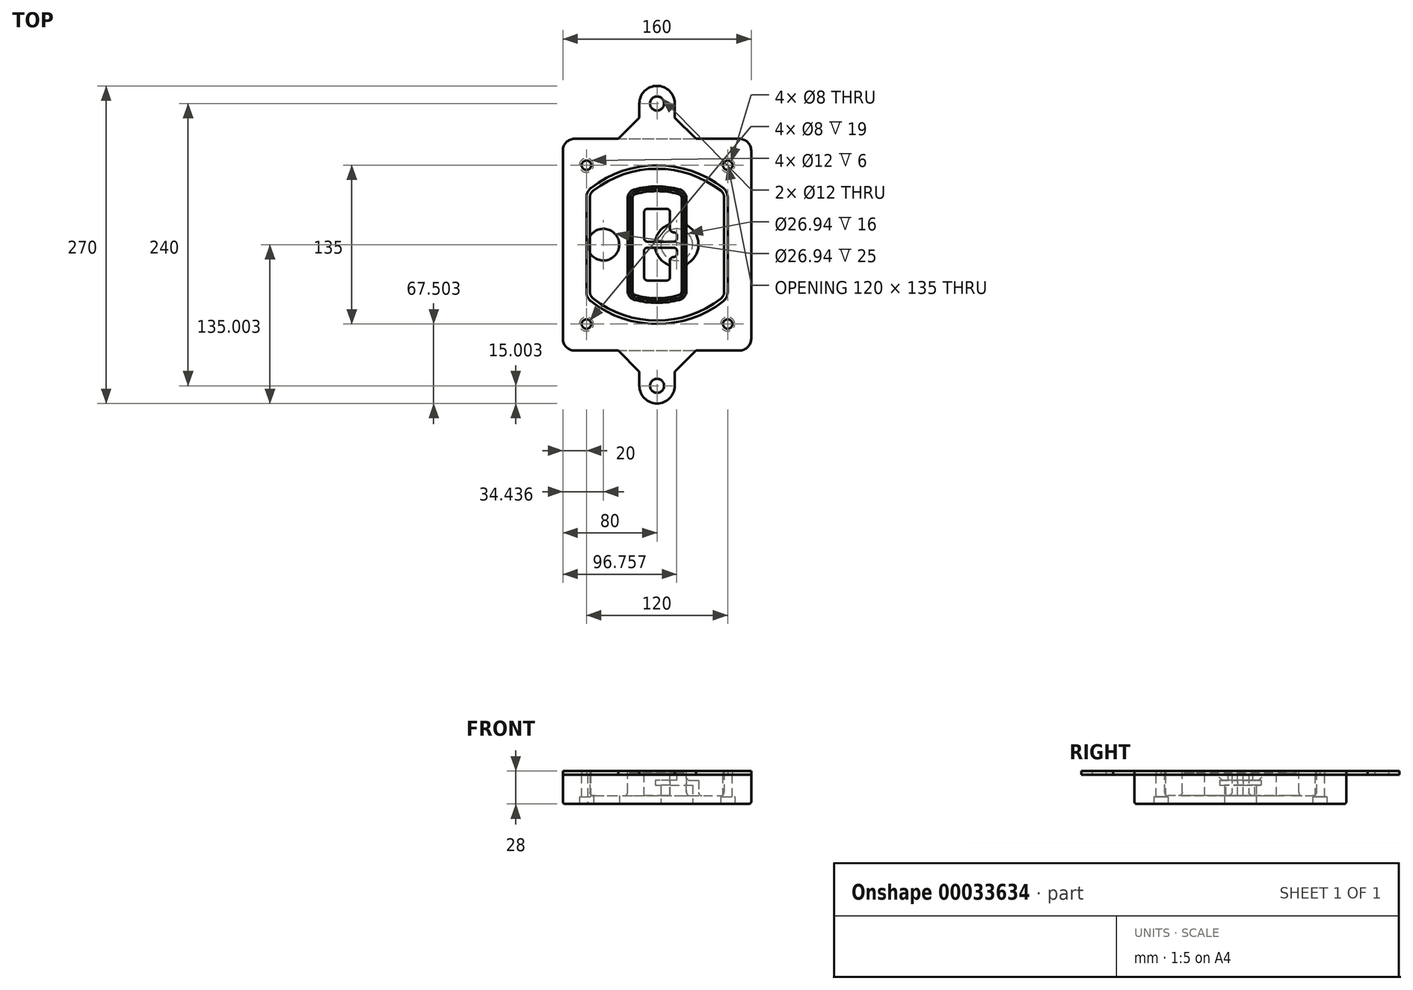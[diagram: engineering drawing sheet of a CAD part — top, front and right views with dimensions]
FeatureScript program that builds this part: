
annotation { "Feature Type Name" : "Feature", "Feature Type Description" : "" }
export const myFeature = defineFeature(function(context is Context, id is Id, definition is map)
    precondition{}
    {
        {
            var Q0;
            Q0=qCreatedBy(makeId("Top.planeOp"),FACE);
            var sketch = newSketch(context, id + "F0", { "sketchPlane" : qUnion([Q0])});
            skPoint(sketch, "E0.rect.middle", {"position": v(0, 0) * mm});
            skLineSegment(sketch, "E1.bottom", {"start": v(24.05, 28.38) * mm, "end": v(164.05, 28.38) * mm});
            skLineSegment(sketch, "E1.top", {"start": v(24.05, 208.38) * mm, "end": v(164.05, 208.38) * mm});
            skLineSegment(sketch, "E1.left", {"start": v(14.05, 38.38) * mm, "end": v(14.05, 198.38) * mm});
            skLineSegment(sketch, "E1.right", {"start": v(174.05, 38.38) * mm, "end": v(174.05, 198.38) * mm});
            skLineSegment(sketch, "E2", {"start": v(14.05, 208.38) * mm, "end": v(174.05, 28.38) * mm, "construction": true});
            skLineSegment(sketch, "E3", {"start": v(174.05, 208.38) * mm, "end": v(14.05, 28.38) * mm, "construction": true});
            skCircle(sketch, "E4", {"center": v(34.05, 185.88) * mm, "radius": 4 * mm});
            skCircle(sketch, "E5", {"center": v(154.05, 185.88) * mm, "radius": 4 * mm});
            skCircle(sketch, "E6", {"center": v(154.05, 50.88) * mm, "radius": 4 * mm});
            skCircle(sketch, "E7", {"center": v(34.05, 50.88) * mm, "radius": 4 * mm});
            skLineSegment(sketch, "E8", {"start": v(34.05, 185.88) * mm, "end": v(154.05, 185.88) * mm, "construction": true});
            skLineSegment(sketch, "E9", {"start": v(154.05, 185.88) * mm, "end": v(154.05, 50.88) * mm, "construction": true});
            skLineSegment(sketch, "E10", {"start": v(154.05, 50.88) * mm, "end": v(34.05, 50.88) * mm, "construction": true});
            skLineSegment(sketch, "E11", {"start": v(34.05, 50.88) * mm, "end": v(34.05, 185.88) * mm, "construction": true});
            skLineSegment(sketch, "E12", {"start": v(34.05, 158.68) * mm, "end": v(34.05, 78.09) * mm});
            skLineSegment(sketch, "E13", {"start": v(154.05, 158.68) * mm, "end": v(154.05, 78.09) * mm});
            skArc(sketch, "E14", {"start": v(150.2, 166.56) * mm, "mid": v(94.05, 185.88) * mm, "end": v(37.9, 166.56) * mm});
            skArc(sketch, "E15", {"start": v(37.9, 70.2) * mm, "mid": v(94.05, 50.88) * mm, "end": v(150.2, 70.2) * mm});
            skLineSegment(sketch, "E16", {"start": v(34.05, 118.38) * mm, "end": v(154.05, 118.38) * mm, "construction": true});
            skPoint(sketch, "E17.visualSharp", {"position": v(34.05, 73.38) * mm});
            skArc(sketch, "E17.filletArc", {"start": v(34.05, 78.09) * mm, "mid": v(35.06, 73.7) * mm, "end": v(37.9, 70.2) * mm});
            skPoint(sketch, "E18.visualSharp", {"position": v(34.05, 163.38) * mm});
            skArc(sketch, "E18.filletArc", {"start": v(37.9, 166.56) * mm, "mid": v(35.06, 163.06) * mm, "end": v(34.05, 158.68) * mm});
            skPoint(sketch, "E19.visualSharp", {"position": v(154.05, 163.38) * mm});
            skArc(sketch, "E19.filletArc", {"start": v(154.05, 158.68) * mm, "mid": v(153.04, 163.06) * mm, "end": v(150.2, 166.56) * mm});
            skPoint(sketch, "E20.visualSharp", {"position": v(154.05, 73.38) * mm});
            skArc(sketch, "E20.filletArc", {"start": v(150.2, 70.2) * mm, "mid": v(153.04, 73.7) * mm, "end": v(154.05, 78.09) * mm});
            skPoint(sketch, "E21.visualSharp", {"position": v(14.05, 208.38) * mm});
            skArc(sketch, "E21.filletArc", {"start": v(24.05, 208.38) * mm, "mid": v(16.98, 205.45) * mm, "end": v(14.05, 198.38) * mm});
            skPoint(sketch, "E22.visualSharp", {"position": v(174.05, 208.38) * mm});
            skArc(sketch, "E22.filletArc", {"start": v(174.05, 198.38) * mm, "mid": v(171.12, 205.45) * mm, "end": v(164.05, 208.38) * mm});
            skPoint(sketch, "E23.visualSharp", {"position": v(174.05, 28.38) * mm});
            skArc(sketch, "E23.filletArc", {"start": v(164.05, 28.38) * mm, "mid": v(171.12, 31.31) * mm, "end": v(174.05, 38.38) * mm});
            skPoint(sketch, "E24.visualSharp", {"position": v(14.05, 28.38) * mm});
            skArc(sketch, "E24.filletArc", {"start": v(14.05, 38.38) * mm, "mid": v(16.98, 31.31) * mm, "end": v(24.05, 28.38) * mm});
            skArc(sketch, "E25.0", {"start": v(151.05, 158.68) * mm, "mid": v(150.34, 161.75) * mm, "end": v(148.36, 164.2) * mm});
            skLineSegment(sketch, "E25.1", {"start": v(151.05, 158.68) * mm, "end": v(151.05, 78.09) * mm});
            skArc(sketch, "E25.2", {"start": v(148.36, 72.57) * mm, "mid": v(150.34, 75.02) * mm, "end": v(151.05, 78.09) * mm});
            skArc(sketch, "E25.3", {"start": v(39.74, 72.57) * mm, "mid": v(94.05, 53.88) * mm, "end": v(148.36, 72.57) * mm});
            skArc(sketch, "E25.4", {"start": v(37.05, 78.09) * mm, "mid": v(37.76, 75.02) * mm, "end": v(39.74, 72.57) * mm});
            skArc(sketch, "E25.5", {"start": v(148.36, 164.2) * mm, "mid": v(94.05, 182.88) * mm, "end": v(39.74, 164.2) * mm});
            skLineSegment(sketch, "E25.6", {"start": v(37.05, 158.68) * mm, "end": v(37.05, 78.09) * mm});
            skArc(sketch, "E25.7", {"start": v(39.74, 164.2) * mm, "mid": v(37.76, 161.75) * mm, "end": v(37.05, 158.68) * mm});
            skArc(sketch, "E26.0", {"start": v(35.43, 169.71) * mm, "mid": v(31.47, 164.82) * mm, "end": v(30.05, 158.68) * mm});
            skArc(sketch, "E26.1", {"start": v(152.67, 169.71) * mm, "mid": v(94.05, 189.88) * mm, "end": v(35.43, 169.71) * mm});
            skArc(sketch, "E26.2", {"start": v(158.05, 158.68) * mm, "mid": v(156.63, 164.82) * mm, "end": v(152.67, 169.71) * mm});
            skLineSegment(sketch, "E26.3", {"start": v(158.05, 158.68) * mm, "end": v(158.05, 78.09) * mm});
            skArc(sketch, "E26.4", {"start": v(152.67, 67.05) * mm, "mid": v(156.63, 71.95) * mm, "end": v(158.05, 78.09) * mm});
            skLineSegment(sketch, "E26.5", {"start": v(30.05, 158.68) * mm, "end": v(30.05, 78.09) * mm});
            skArc(sketch, "E26.6", {"start": v(35.43, 67.05) * mm, "mid": v(94.05, 46.88) * mm, "end": v(152.67, 67.05) * mm});
            skArc(sketch, "E26.7", {"start": v(30.05, 78.09) * mm, "mid": v(31.47, 71.95) * mm, "end": v(35.43, 67.05) * mm});
            skSolve(sketch);
        }
        {
            var Q0;
            Q0=makeQuery(id+"F0.imprint","IMPRINT",FACE,{"disambiguationData":[TD([[makeQuery(id+"F0.imprint","IMPRINT",EDGE,{"derivedFrom":sQuery(id+"F0.wireOp",EDGE,"E1.bottom")}),1.0]])]});
            var Q1;
            Q1=makeQuery(id+"F0.imprint","IMPRINT",FACE,{"disambiguationData":[TD([[makeQuery(id+"F0.imprint","IMPRINT",EDGE,{"derivedFrom":sQuery(id+"F0.wireOp",EDGE,"E12")}),1.0]])]});
            var Q2;
            Q2=makeQuery(id+"F0.imprint","IMPRINT",FACE,{"disambiguationData":[TD([[makeQuery(id+"F0.imprint","IMPRINT",EDGE,{"derivedFrom":sQuery(id+"F0.wireOp",EDGE,"E25.0")}),1.0]])]});
            var Q3;
            Q3=makeQuery(id+"F0.imprint","IMPRINT",FACE,{"disambiguationData":[TD([[makeQuery(id+"F0.imprint","IMPRINT",EDGE,{"derivedFrom":sQuery(id+"F0.wireOp",EDGE,"E12")}),-1.0]])]});
            extrude(context, id + "F1", {"entities" : qUnion([Q0, Q1, Q2, Q3]), "oppositeDirection" : true, "depth" : 25 * mm});
        }
        {
            var Q0;
            Q0=makeQuery(id+"F0.imprint","IMPRINT",FACE,{"disambiguationData":[TD([[makeQuery(id+"F0.imprint","IMPRINT",EDGE,{"derivedFrom":sQuery(id+"F0.wireOp",EDGE,"E12")}),1.0]])]});
            extrude(context, id + "F2", {"entities" : qUnion([Q0]), "operationType" : NewBodyOperationType.ADD, "depth" : 3 * mm});
        }
        {
            var Q0;
            Q0=makeQuery(id+"F0.imprint","IMPRINT",FACE,{"disambiguationData":[TD([[makeQuery(id+"F0.imprint","IMPRINT",EDGE,{"derivedFrom":sQuery(id+"F0.wireOp",EDGE,"E25.0")}),1.0]])]});
            extrude(context, id + "F3", {"entities" : qUnion([Q0]), "operationType" : NewBodyOperationType.REMOVE, "oppositeDirection" : true, "depth" : 18 * mm});
        }
        {
            var Q0;
            Q0=makeQuery(id+"F2.opExtrude","CAP_FACE",FACE,{"disambiguationData":[OSD([sQuery(id+"F0.wireOp",EDGE,"E12"),sQuery(id+"F0.wireOp",EDGE,"E13"),sQuery(id+"F0.wireOp",EDGE,"E14"),sQuery(id+"F0.wireOp",EDGE,"E15"),sQuery(id+"F0.wireOp",EDGE,"E17.filletArc"),sQuery(id+"F0.wireOp",EDGE,"E18.filletArc"),sQuery(id+"F0.wireOp",EDGE,"E19.filletArc"),sQuery(id+"F0.wireOp",EDGE,"E20.filletArc"),sQuery(id+"F0.wireOp",EDGE,"E25.0"),sQuery(id+"F0.wireOp",EDGE,"E25.1"),sQuery(id+"F0.wireOp",EDGE,"E25.2"),sQuery(id+"F0.wireOp",EDGE,"E25.3"),sQuery(id+"F0.wireOp",EDGE,"E25.4"),sQuery(id+"F0.wireOp",EDGE,"E25.5"),sQuery(id+"F0.wireOp",EDGE,"E25.6"),sQuery(id+"F0.wireOp",EDGE,"E25.7")])],"isStart":false});
            var sketch = newSketch(context, id + "F4", { "sketchPlane" : qUnion([Q0])});
            skArc(sketch, "E27.0", {"start": v(74.97, 71.41) * mm, "mid": v(94.05, 68.88) * mm, "end": v(113.13, 71.41) * mm});
            skArc(sketch, "E28.0", {"start": v(113.13, 165.35) * mm, "mid": v(94.05, 167.88) * mm, "end": v(74.97, 165.35) * mm});
            skLineSegment(sketch, "E29", {"start": v(69.05, 157.63) * mm, "end": v(69.05, 79.14) * mm});
            skLineSegment(sketch, "E30", {"start": v(119.05, 157.63) * mm, "end": v(119.05, 79.14) * mm});
            skLineSegment(sketch, "E31", {"start": v(69.05, 163.48) * mm, "end": v(119.05, 163.48) * mm, "construction": true});
            skLineSegment(sketch, "E32", {"start": v(69.05, 73.28) * mm, "end": v(119.05, 73.28) * mm, "construction": true});
            skPoint(sketch, "E33.visualSharp", {"position": v(69.05, 163.48) * mm});
            skArc(sketch, "E33.filletArc", {"start": v(74.97, 165.35) * mm, "mid": v(70.7, 162.5) * mm, "end": v(69.05, 157.63) * mm});
            skPoint(sketch, "E34.visualSharp", {"position": v(119.05, 163.48) * mm});
            skArc(sketch, "E34.filletArc", {"start": v(119.05, 157.63) * mm, "mid": v(117.4, 162.5) * mm, "end": v(113.13, 165.35) * mm});
            skPoint(sketch, "E35.visualSharp", {"position": v(119.05, 73.28) * mm});
            skArc(sketch, "E35.filletArc", {"start": v(113.13, 71.41) * mm, "mid": v(117.4, 74.27) * mm, "end": v(119.05, 79.14) * mm});
            skPoint(sketch, "E36.visualSharp", {"position": v(69.05, 73.28) * mm});
            skArc(sketch, "E36.filletArc", {"start": v(69.05, 79.14) * mm, "mid": v(70.7, 74.27) * mm, "end": v(74.97, 71.41) * mm});
            skArc(sketch, "E37.0", {"start": v(148.36, 164.2) * mm, "mid": v(94.05, 182.88) * mm, "end": v(39.74, 164.2) * mm});
            skArc(sketch, "E37.1", {"start": v(39.74, 164.2) * mm, "mid": v(37.76, 161.75) * mm, "end": v(37.05, 158.68) * mm});
            skLineSegment(sketch, "E37.2", {"start": v(37.05, 158.68) * mm, "end": v(37.05, 78.09) * mm});
            skArc(sketch, "E37.3", {"start": v(37.05, 78.09) * mm, "mid": v(37.76, 75.02) * mm, "end": v(39.74, 72.57) * mm});
            skArc(sketch, "E37.4", {"start": v(39.74, 72.57) * mm, "mid": v(94.05, 53.88) * mm, "end": v(148.36, 72.57) * mm});
            skArc(sketch, "E37.5", {"start": v(148.36, 72.57) * mm, "mid": v(150.34, 75.02) * mm, "end": v(151.05, 78.09) * mm});
            skLineSegment(sketch, "E37.6", {"start": v(151.05, 158.68) * mm, "end": v(151.05, 78.09) * mm});
            skArc(sketch, "E37.7", {"start": v(151.05, 158.68) * mm, "mid": v(150.34, 161.75) * mm, "end": v(148.36, 164.2) * mm});
            skLineSegment(sketch, "E38.0", {"start": v(117.05, 157.63) * mm, "end": v(117.05, 79.14) * mm});
            skArc(sketch, "E38.1", {"start": v(112.61, 73.34) * mm, "mid": v(115.81, 75.49) * mm, "end": v(117.05, 79.14) * mm});
            skArc(sketch, "E38.2", {"start": v(75.49, 73.34) * mm, "mid": v(94.05, 70.88) * mm, "end": v(112.61, 73.34) * mm});
            skArc(sketch, "E38.3", {"start": v(71.05, 79.14) * mm, "mid": v(72.29, 75.49) * mm, "end": v(75.49, 73.34) * mm});
            skLineSegment(sketch, "E38.4", {"start": v(71.05, 157.63) * mm, "end": v(71.05, 79.14) * mm});
            skArc(sketch, "E38.5", {"start": v(117.05, 157.63) * mm, "mid": v(115.81, 161.28) * mm, "end": v(112.61, 163.42) * mm});
            skArc(sketch, "E38.6", {"start": v(75.49, 163.42) * mm, "mid": v(72.29, 161.28) * mm, "end": v(71.05, 157.63) * mm});
            skArc(sketch, "E38.7", {"start": v(112.61, 163.42) * mm, "mid": v(94.05, 165.88) * mm, "end": v(75.49, 163.42) * mm});
            skArc(sketch, "E39.0", {"start": v(115.05, 157.63) * mm, "mid": v(114.23, 160.06) * mm, "end": v(112.1, 161.5) * mm});
            skLineSegment(sketch, "E39.1", {"start": v(115.05, 157.63) * mm, "end": v(115.05, 79.14) * mm});
            skArc(sketch, "E39.2", {"start": v(112.1, 75.27) * mm, "mid": v(114.23, 76.7) * mm, "end": v(115.05, 79.14) * mm});
            skArc(sketch, "E39.3", {"start": v(76, 75.27) * mm, "mid": v(94.05, 72.88) * mm, "end": v(112.1, 75.27) * mm});
            skArc(sketch, "E39.4", {"start": v(73.05, 79.14) * mm, "mid": v(73.87, 76.7) * mm, "end": v(76, 75.27) * mm});
            skArc(sketch, "E39.5", {"start": v(112.1, 161.5) * mm, "mid": v(94.05, 163.88) * mm, "end": v(76, 161.5) * mm});
            skLineSegment(sketch, "E39.6", {"start": v(73.05, 157.63) * mm, "end": v(73.05, 79.14) * mm});
            skArc(sketch, "E39.7", {"start": v(76, 161.5) * mm, "mid": v(73.87, 160.06) * mm, "end": v(73.05, 157.63) * mm});
            skLineSegment(sketch, "E40", {"start": v(69.05, 118.38) * mm, "end": v(119.05, 118.38) * mm, "construction": true});
            skLineSegment(sketch, "E41", {"start": v(83.05, 123.88) * mm, "end": v(83.05, 145.88) * mm});
            skLineSegment(sketch, "E42", {"start": v(86.05, 148.88) * mm, "end": v(102.05, 148.88) * mm});
            skLineSegment(sketch, "E43", {"start": v(105.05, 145.88) * mm, "end": v(105.05, 131.88) * mm});
            skLineSegment(sketch, "E44", {"start": v(108.05, 128.88) * mm, "end": v(108.05, 128.88) * mm});
            skLineSegment(sketch, "E45", {"start": v(111.05, 125.88) * mm, "end": v(111.05, 123.88) * mm});
            skLineSegment(sketch, "E46", {"start": v(108.05, 120.88) * mm, "end": v(86.05, 120.88) * mm});
            skPoint(sketch, "E47.visualSharp", {"position": v(83.05, 148.88) * mm});
            skArc(sketch, "E47.filletArc", {"start": v(86.05, 148.88) * mm, "mid": v(83.93, 148) * mm, "end": v(83.05, 145.88) * mm});
            skPoint(sketch, "E48.visualSharp", {"position": v(105.05, 148.88) * mm});
            skArc(sketch, "E48.filletArc", {"start": v(105.05, 145.88) * mm, "mid": v(104.17, 148) * mm, "end": v(102.05, 148.88) * mm});
            skPoint(sketch, "E49.visualSharp", {"position": v(105.05, 128.88) * mm});
            skArc(sketch, "E49.filletArc", {"start": v(105.05, 131.88) * mm, "mid": v(105.93, 129.76) * mm, "end": v(108.05, 128.88) * mm});
            skPoint(sketch, "E50.visualSharp", {"position": v(111.05, 128.88) * mm});
            skArc(sketch, "E50.filletArc", {"start": v(111.05, 125.88) * mm, "mid": v(110.17, 128) * mm, "end": v(108.05, 128.88) * mm});
            skPoint(sketch, "E51.visualSharp", {"position": v(111.05, 120.88) * mm});
            skArc(sketch, "E51.filletArc", {"start": v(108.05, 120.88) * mm, "mid": v(110.17, 121.76) * mm, "end": v(111.05, 123.88) * mm});
            skPoint(sketch, "E52.visualSharp", {"position": v(83.05, 120.88) * mm});
            skArc(sketch, "E52.filletArc", {"start": v(83.05, 123.88) * mm, "mid": v(83.93, 121.76) * mm, "end": v(86.05, 120.88) * mm});
            skLineSegment(sketch, "E53.0.MirrorCS", {"start": v(108.05, 115.88) * mm, "end": v(86.05, 115.88) * mm});
            skArc(sketch, "E54.0.MirrorCS", {"start": v(83.05, 112.88) * mm, "mid": v(83.93, 115) * mm, "end": v(86.05, 115.88) * mm});
            skLineSegment(sketch, "E55.0.MirrorCS", {"start": v(83.05, 112.88) * mm, "end": v(83.05, 90.88) * mm});
            skArc(sketch, "E56.0.MirrorCS", {"start": v(86.05, 87.88) * mm, "mid": v(83.93, 88.76) * mm, "end": v(83.05, 90.88) * mm});
            skLineSegment(sketch, "E57.0.MirrorCS", {"start": v(86.05, 87.88) * mm, "end": v(102.05, 87.88) * mm});
            skArc(sketch, "E58.0.MirrorCS", {"start": v(105.05, 90.88) * mm, "mid": v(104.17, 88.76) * mm, "end": v(102.05, 87.88) * mm});
            skLineSegment(sketch, "E59.0.MirrorCS", {"start": v(105.05, 90.88) * mm, "end": v(105.05, 104.88) * mm});
            skArc(sketch, "E60.0.MirrorCS", {"start": v(105.05, 104.88) * mm, "mid": v(105.93, 107) * mm, "end": v(108.05, 107.88) * mm});
            skArc(sketch, "E61.0.MirrorCS", {"start": v(111.05, 110.88) * mm, "mid": v(110.17, 108.76) * mm, "end": v(108.05, 107.88) * mm});
            skLineSegment(sketch, "E62.0.MirrorCS", {"start": v(111.05, 110.88) * mm, "end": v(111.05, 112.88) * mm});
            skArc(sketch, "E63.0.MirrorCS", {"start": v(108.05, 115.88) * mm, "mid": v(110.17, 115) * mm, "end": v(111.05, 112.88) * mm});
            skSolve(sketch);
        }
        {
            var Q0;
            Q0=makeQuery(id+"F4.imprint","IMPRINT",FACE,{"disambiguationData":[TD([[makeQuery(id+"F4.imprint","IMPRINT",EDGE,{"derivedFrom":sQuery(id+"F4.wireOp",EDGE,"E27.0")}),1.0]])]});
            var Q1;
            Q1=makeQuery(id+"F4.imprint","IMPRINT",FACE,{"disambiguationData":[TD([[makeQuery(id+"F4.imprint","IMPRINT",EDGE,{"derivedFrom":sQuery(id+"F4.wireOp",EDGE,"E38.0")}),-1.0]])]});
            var Q2;
            Q2=makeQuery(id+"F4.imprint","IMPRINT",FACE,{"disambiguationData":[TD([[makeQuery(id+"F4.imprint","IMPRINT",EDGE,{"derivedFrom":sQuery(id+"F4.wireOp",EDGE,"E39.0")}),1.0]])]});
            extrude(context, id + "F5", {"entities" : qUnion([Q0, Q1, Q2]), "operationType" : NewBodyOperationType.ADD, "endBound" : BoundingType.UP_TO_NEXT, "oppositeDirection" : true, "depth" : 25 * mm});
        }
        {
            var Q0;
            Q0=makeQuery(id+"F4.imprint","IMPRINT",FACE,{"disambiguationData":[TD([[makeQuery(id+"F4.imprint","IMPRINT",EDGE,{"derivedFrom":sQuery(id+"F4.wireOp",EDGE,"E38.0")}),-1.0]])]});
            extrude(context, id + "F6", {"entities" : qUnion([Q0]), "operationType" : NewBodyOperationType.REMOVE, "oppositeDirection" : true, "depth" : 2 * mm});
        }
        {
            var Q0;
            Q0=makeQuery(id+"F1.opExtrude","CAP_FACE",FACE,{"disambiguationData":[OSD([sQuery(id+"F0.wireOp",EDGE,"E1.bottom"),sQuery(id+"F0.wireOp",EDGE,"E1.top"),sQuery(id+"F0.wireOp",EDGE,"E1.left"),sQuery(id+"F0.wireOp",EDGE,"E1.right"),sQuery(id+"F0.wireOp",EDGE,"E4"),sQuery(id+"F0.wireOp",EDGE,"E5"),sQuery(id+"F0.wireOp",EDGE,"E6"),sQuery(id+"F0.wireOp",EDGE,"E7"),sQuery(id+"F0.wireOp",EDGE,"E21.filletArc"),sQuery(id+"F0.wireOp",EDGE,"E22.filletArc"),sQuery(id+"F0.wireOp",EDGE,"E23.filletArc"),sQuery(id+"F0.wireOp",EDGE,"E24.filletArc")])],"isStart":false});
            var sketch = newSketch(context, id + "F7", { "sketchPlane" : qUnion([Q0])});
            skCircle(sketch, "E64", {"center": v(110.8, -118.38) * mm, "radius": 13.47 * mm});
            skCircle(sketch, "E65", {"center": v(48.49, -118.38) * mm, "radius": 13.47 * mm});
            skLineSegment(sketch, "E66", {"start": v(174.05, -118.38) * mm, "end": v(14.05, -118.38) * mm});
            skCircle(sketch, "E67", {"center": v(110.8, -118.38) * mm, "radius": 18.47 * mm});
            skCircle(sketch, "E68", {"center": v(154.05, -185.88) * mm, "radius": 6 * mm});
            skCircle(sketch, "E69", {"center": v(34.05, -185.88) * mm, "radius": 6 * mm});
            skCircle(sketch, "E70", {"center": v(34.05, -50.88) * mm, "radius": 6 * mm});
            skCircle(sketch, "E71", {"center": v(154.05, -50.88) * mm, "radius": 6 * mm});
            skSolve(sketch);
        }
        {
            var Q0;
            {var subQ1=sQuery(id+"F7.wireOp",EDGE,"E66");var subQ4=sQuery(id+"F7.wireOp",EDGE,"E64");var subQ6=makeQuery(id+"F7.imprint","INTERSECT",VERTEX,{"disambiguationData":[OD(0.0)],"derivedFrom":[subQ4,subQ1]});Q0=makeQuery(id+"F7.imprint","IMPRINT",FACE,{"disambiguationData":[TD([[makeQuery(id+"F7.imprint","IMPRINT",EDGE,{"disambiguationData":[TD([[subQ6,-1.0]])],"derivedFrom":subQ4}),-1.0]])]});}
            var Q1;
            {var subQ0=sQuery(id+"F7.wireOp",EDGE,"E66");var subQ1=sQuery(id+"F7.wireOp",EDGE,"E64");var subQ3=makeQuery(id+"F7.imprint","INTERSECT",VERTEX,{"disambiguationData":[OD(0.0)],"derivedFrom":[subQ1,subQ0]});Q1=makeQuery(id+"F7.imprint","IMPRINT",FACE,{"disambiguationData":[TD([[makeQuery(id+"F7.imprint","IMPRINT",EDGE,{"disambiguationData":[TD([[subQ3,-1.0]])],"derivedFrom":subQ1}),1.0]])]});}
            var Q2;
            {var subQ0=sQuery(id+"F7.wireOp",EDGE,"E66");var subQ1=sQuery(id+"F7.wireOp",EDGE,"E64");var subQ3=makeQuery(id+"F7.imprint","INTERSECT",VERTEX,{"disambiguationData":[OD(0.0)],"derivedFrom":[subQ1,subQ0]});Q2=makeQuery(id+"F7.imprint","IMPRINT",FACE,{"disambiguationData":[TD([[makeQuery(id+"F7.imprint","IMPRINT",EDGE,{"disambiguationData":[TD([[subQ3,1.0]])],"derivedFrom":subQ1}),1.0]])]});}
            var Q3;
            {var subQ1=sQuery(id+"F7.wireOp",EDGE,"E66");var subQ4=sQuery(id+"F7.wireOp",EDGE,"E64");var subQ6=makeQuery(id+"F7.imprint","INTERSECT",VERTEX,{"disambiguationData":[OD(0.0)],"derivedFrom":[subQ4,subQ1]});Q3=makeQuery(id+"F7.imprint","IMPRINT",FACE,{"disambiguationData":[TD([[makeQuery(id+"F7.imprint","IMPRINT",EDGE,{"disambiguationData":[TD([[subQ6,1.0]])],"derivedFrom":subQ4}),-1.0]])]});}
            extrude(context, id + "F8", {"entities" : qUnion([Q0, Q1, Q2, Q3]), "operationType" : NewBodyOperationType.ADD, "oppositeDirection" : true, "depth" : 20 * mm});
        }
        {
            var Q0;
            {var subQ0=sQuery(id+"F7.wireOp",EDGE,"E66");var subQ1=sQuery(id+"F7.wireOp",EDGE,"E64");var subQ3=makeQuery(id+"F7.imprint","INTERSECT",VERTEX,{"disambiguationData":[OD(0.0)],"derivedFrom":[subQ1,subQ0]});Q0=makeQuery(id+"F7.imprint","IMPRINT",FACE,{"disambiguationData":[TD([[makeQuery(id+"F7.imprint","IMPRINT",EDGE,{"disambiguationData":[TD([[subQ3,-1.0]])],"derivedFrom":subQ1}),1.0]])]});}
            var Q1;
            {var subQ0=sQuery(id+"F7.wireOp",EDGE,"E66");var subQ1=sQuery(id+"F7.wireOp",EDGE,"E64");var subQ3=makeQuery(id+"F7.imprint","INTERSECT",VERTEX,{"disambiguationData":[OD(0.0)],"derivedFrom":[subQ1,subQ0]});Q1=makeQuery(id+"F7.imprint","IMPRINT",FACE,{"disambiguationData":[TD([[makeQuery(id+"F7.imprint","IMPRINT",EDGE,{"disambiguationData":[TD([[subQ3,1.0]])],"derivedFrom":subQ1}),1.0]])]});}
            extrude(context, id + "F9", {"entities" : qUnion([Q0, Q1]), "operationType" : NewBodyOperationType.REMOVE, "oppositeDirection" : true, "depth" : 16 * mm});
        }
        {
            var Q0;
            {var subQ0=sQuery(id+"F7.wireOp",EDGE,"E66");var subQ1=sQuery(id+"F7.wireOp",EDGE,"E65");var subQ3=makeQuery(id+"F7.imprint","INTERSECT",VERTEX,{"disambiguationData":[OD(0.0)],"derivedFrom":[subQ1,subQ0]});Q0=makeQuery(id+"F7.imprint","IMPRINT",FACE,{"disambiguationData":[TD([[makeQuery(id+"F7.imprint","IMPRINT",EDGE,{"disambiguationData":[TD([[subQ3,-1.0]])],"derivedFrom":subQ1}),1.0]])]});}
            var Q1;
            {var subQ0=sQuery(id+"F7.wireOp",EDGE,"E66");var subQ1=sQuery(id+"F7.wireOp",EDGE,"E65");var subQ3=makeQuery(id+"F7.imprint","INTERSECT",VERTEX,{"disambiguationData":[OD(0.0)],"derivedFrom":[subQ1,subQ0]});Q1=makeQuery(id+"F7.imprint","IMPRINT",FACE,{"disambiguationData":[TD([[makeQuery(id+"F7.imprint","IMPRINT",EDGE,{"disambiguationData":[TD([[subQ3,1.0]])],"derivedFrom":subQ1}),1.0]])]});}
            extrude(context, id + "F10", {"entities" : qUnion([Q0, Q1]), "operationType" : NewBodyOperationType.REMOVE, "oppositeDirection" : true, "depth" : 25 * mm});
        }
        {
            var Q0;
            Q0=makeQuery(id+"F7.imprint","IMPRINT",FACE,{"disambiguationData":[TD([[makeQuery(id+"F7.imprint","IMPRINT",EDGE,{"derivedFrom":sQuery(id+"F7.wireOp",EDGE,"E68")}),1.0]])]});
            var Q1;
            Q1=makeQuery(id+"F7.imprint","IMPRINT",FACE,{"disambiguationData":[TD([[makeQuery(id+"F7.imprint","IMPRINT",EDGE,{"derivedFrom":makeQuery(id+"F1.opExtrude","CAP_EDGE",EDGE,{"disambiguationData":[OSD([sQuery(id+"F0.wireOp",EDGE,"E5")])],"isStart":false})}),-1.0]])]});
            var Q2;
            Q2=makeQuery(id+"F7.imprint","IMPRINT",FACE,{"disambiguationData":[TD([[makeQuery(id+"F7.imprint","IMPRINT",EDGE,{"derivedFrom":sQuery(id+"F7.wireOp",EDGE,"E69")}),1.0]])]});
            var Q3;
            Q3=makeQuery(id+"F7.imprint","IMPRINT",FACE,{"disambiguationData":[TD([[makeQuery(id+"F7.imprint","IMPRINT",EDGE,{"derivedFrom":makeQuery(id+"F1.opExtrude","CAP_EDGE",EDGE,{"disambiguationData":[OSD([sQuery(id+"F0.wireOp",EDGE,"E4")])],"isStart":false})}),-1.0]])]});
            var Q4;
            Q4=makeQuery(id+"F7.imprint","IMPRINT",FACE,{"disambiguationData":[TD([[makeQuery(id+"F7.imprint","IMPRINT",EDGE,{"derivedFrom":sQuery(id+"F7.wireOp",EDGE,"E70")}),1.0]])]});
            var Q5;
            Q5=makeQuery(id+"F7.imprint","IMPRINT",FACE,{"disambiguationData":[TD([[makeQuery(id+"F7.imprint","IMPRINT",EDGE,{"derivedFrom":makeQuery(id+"F1.opExtrude","CAP_EDGE",EDGE,{"disambiguationData":[OSD([sQuery(id+"F0.wireOp",EDGE,"E7")])],"isStart":false})}),-1.0]])]});
            var Q6;
            Q6=makeQuery(id+"F7.imprint","IMPRINT",FACE,{"disambiguationData":[TD([[makeQuery(id+"F7.imprint","IMPRINT",EDGE,{"derivedFrom":sQuery(id+"F7.wireOp",EDGE,"E71")}),1.0]])]});
            var Q7;
            Q7=makeQuery(id+"F7.imprint","IMPRINT",FACE,{"disambiguationData":[TD([[makeQuery(id+"F7.imprint","IMPRINT",EDGE,{"derivedFrom":makeQuery(id+"F1.opExtrude","CAP_EDGE",EDGE,{"disambiguationData":[OSD([sQuery(id+"F0.wireOp",EDGE,"E6")])],"isStart":false})}),-1.0]])]});
            extrude(context, id + "F11", {"entities" : qUnion([Q0, Q1, Q2, Q3, Q4, Q5, Q6, Q7]), "operationType" : NewBodyOperationType.REMOVE, "oppositeDirection" : true, "depth" : 6 * mm});
        }
        {
            var Q0;
            Q0=makeQuery(id+"F9.boolean.opBoolean","COPY",FACE,{"derivedFrom":makeQuery(id+"F9.opExtrude","CAP_FACE",FACE,{"disambiguationData":[OSD([sQuery(id+"F7.wireOp",EDGE,"E64")])],"isStart":false})});
            var sketch = newSketch(context, id + "F12", { "sketchPlane" : qUnion([Q0])});
            skArc(sketch, "E72.0", {"start": v(105.05, -100.83) * mm, "mid": v(96.62, -106.56) * mm, "end": v(92.5, -115.88) * mm});
            skArc(sketch, "E72.1", {"start": v(92.5, -120.88) * mm, "mid": v(96.62, -130.2) * mm, "end": v(105.05, -135.93) * mm});
            skLineSegment(sketch, "E73", {"start": v(92.5, -120.88) * mm, "end": v(108.05, -120.88) * mm});
            skLineSegment(sketch, "E74.0", {"start": v(108.05, -115.88) * mm, "end": v(92.5, -115.88) * mm});
            skArc(sketch, "E74.1", {"start": v(108.05, -115.88) * mm, "mid": v(110.17, -115) * mm, "end": v(111.05, -112.88) * mm});
            skLineSegment(sketch, "E74.2", {"start": v(111.05, -110.88) * mm, "end": v(111.05, -112.88) * mm});
            skArc(sketch, "E74.3", {"start": v(111.05, -110.88) * mm, "mid": v(110.17, -108.76) * mm, "end": v(108.05, -107.88) * mm});
            skArc(sketch, "E74.4", {"start": v(105.05, -104.88) * mm, "mid": v(105.93, -107) * mm, "end": v(108.05, -107.88) * mm});
            skLineSegment(sketch, "E74.5", {"start": v(105.05, -100.83) * mm, "end": v(105.05, -104.88) * mm});
            skLineSegment(sketch, "E74.7", {"start": v(108.05, -120.88) * mm, "end": v(92.5, -120.88) * mm});
            skArc(sketch, "E74.8", {"start": v(108.05, -120.88) * mm, "mid": v(110.17, -121.76) * mm, "end": v(111.05, -123.88) * mm});
            skLineSegment(sketch, "E74.9", {"start": v(111.05, -125.88) * mm, "end": v(111.05, -123.88) * mm});
            skArc(sketch, "E74.10", {"start": v(111.05, -125.88) * mm, "mid": v(110.17, -128) * mm, "end": v(108.05, -128.88) * mm});
            skArc(sketch, "E74.11", {"start": v(105.05, -131.88) * mm, "mid": v(105.93, -129.76) * mm, "end": v(108.05, -128.88) * mm});
            skLineSegment(sketch, "E74.12", {"start": v(105.05, -135.93) * mm, "end": v(105.05, -131.88) * mm});
            skPoint(sketch, "E75.orphan", {"position": v(105.05, -145.88) * mm});
            skPoint(sketch, "E76.orphan", {"position": v(86.05, -120.88) * mm});
            skPoint(sketch, "E77.orphan", {"position": v(86.05, -115.88) * mm});
            skPoint(sketch, "E78.orphan", {"position": v(105.05, -90.88) * mm});
            skSolve(sketch);
        }
        {
            var Q0;
            {var subQ7=sQuery(id+"F12.wireOp",EDGE,"E72.0");var subQ14=sQuery(id+"F12.wireOp",EDGE,"E72.1");var subQ16=sQuery(id+"F12.wireOp",EDGE,"E74.1");var subQ18=sQuery(id+"F12.wireOp",EDGE,"E74.8");Q0=qUnion([makeQuery(id+"F12.imprint","IMPRINT",FACE,{"disambiguationData":[TD([[makeQuery(id+"F12.imprint","IMPRINT",EDGE,{"derivedFrom":subQ7}),1.0]])]}),makeQuery(id+"F12.imprint","IMPRINT",FACE,{"disambiguationData":[TD([[makeQuery(id+"F12.imprint","IMPRINT",EDGE,{"derivedFrom":subQ14}),1.0]])]}),makeQuery(id+"F12.imprint","IMPRINT",FACE,{"disambiguationData":[TD([[makeQuery(id+"F12.imprint","IMPRINT",EDGE,{"derivedFrom":subQ16}),1.0]])]}),makeQuery(id+"F12.imprint","IMPRINT",FACE,{"disambiguationData":[TD([[makeQuery(id+"F12.imprint","IMPRINT",EDGE,{"derivedFrom":subQ18}),-1.0]])]})]);}
            var Q1;
            Q1=makeQuery(id+"F5.boolean.opBoolean","SPLIT",FACE,{"disambiguationData":[TD([makeQuery(id+"F5.opExtrude","SWEPT_FACE",FACE,{"disambiguationData":[OSD([sQuery(id+"F4.wireOp",EDGE,"E41")])]})])],"derivedFrom":makeQuery(id+"F3.boolean.opBoolean","COPY",FACE,{"derivedFrom":makeQuery(id+"F3.opExtrude","CAP_FACE",FACE,{"disambiguationData":[OSD([sQuery(id+"F0.wireOp",EDGE,"E25.0"),sQuery(id+"F0.wireOp",EDGE,"E25.1"),sQuery(id+"F0.wireOp",EDGE,"E25.2"),sQuery(id+"F0.wireOp",EDGE,"E25.3"),sQuery(id+"F0.wireOp",EDGE,"E25.4"),sQuery(id+"F0.wireOp",EDGE,"E25.5"),sQuery(id+"F0.wireOp",EDGE,"E25.6"),sQuery(id+"F0.wireOp",EDGE,"E25.7")])],"isStart":false})})});
            extrude(context, id + "F13", {"entities" : qUnion([Q0]), "operationType" : NewBodyOperationType.REMOVE, "endBound" : BoundingType.UP_TO_SURFACE, "endBoundEntityFace" : qUnion([Q1]), "depth" : 25 * mm});
        }
        {
            var Q0;
            Q0=makeQuery(id+"F3.boolean.opBoolean","COPY",EDGE,{"derivedFrom":makeQuery(id+"F3.opExtrude","CAP_EDGE",EDGE,{"disambiguationData":[OSD([sQuery(id+"F0.wireOp",EDGE,"E25.6")])],"isStart":false})});
            var Q1;
            Q1=makeQuery(id+"F8.boolean.opBoolean","INTERSECT",EDGE,{"derivedFrom":[makeQuery(id+"F5.opExtrude","SWEPT_FACE",FACE,{"disambiguationData":[OSD([sQuery(id+"F4.wireOp",EDGE,"E30")])]}),makeQuery(id+"F8.opExtrude","CAP_FACE",FACE,{"disambiguationData":[OSD([sQuery(id+"F7.wireOp",EDGE,"E67")])],"isStart":false})]});
            var Q2;
            Q2=makeQuery(id+"F8.boolean.opBoolean","INTERSECT",EDGE,{"disambiguationData":[OD(1.0)],"derivedFrom":[makeQuery(id+"F5.opExtrude","SWEPT_FACE",FACE,{"disambiguationData":[OSD([sQuery(id+"F4.wireOp",EDGE,"E30")])]}),makeQuery(id+"F8.opExtrude","SWEPT_FACE",FACE,{"disambiguationData":[OSD([sQuery(id+"F7.wireOp",EDGE,"E67")])]})]});
            var Q3;
            {var subQ0=sQuery(id+"F4.wireOp",EDGE,"E30");Q3=makeQuery(id+"F8.boolean.opBoolean","SPLIT",EDGE,{"disambiguationData":[TD([makeQuery(id+"F5.opExtrude","SWEPT_FACE",FACE,{"disambiguationData":[OSD([sQuery(id+"F4.wireOp",EDGE,"E35.filletArc")])]})])],"derivedFrom":makeQuery(id+"F5.opExtrude","CAP_EDGE",EDGE,{"disambiguationData":[OSD([subQ0])],"isStart":false})});}
            var Q4;
            {var subQ0=sQuery(id+"F0.wireOp",EDGE,"E25.7");var subQ1=sQuery(id+"F0.wireOp",EDGE,"E25.1");var subQ2=sQuery(id+"F0.wireOp",EDGE,"E25.6");var subQ3=sQuery(id+"F0.wireOp",EDGE,"E25.5");var subQ4=sQuery(id+"F0.wireOp",EDGE,"E25.4");var subQ5=sQuery(id+"F0.wireOp",EDGE,"E25.0");var subQ6=sQuery(id+"F0.wireOp",EDGE,"E25.2");var subQ7=sQuery(id+"F0.wireOp",EDGE,"E25.3");Q4=makeQuery(id+"F8.boolean.opBoolean","INTERSECT",EDGE,{"derivedFrom":[makeQuery(id+"F5.boolean.opBoolean","SPLIT",FACE,{"disambiguationData":[TD([makeQuery(id+"F2.opExtrude","SWEPT_FACE",FACE,{"disambiguationData":[OSD([subQ5])]})])],"derivedFrom":makeQuery(id+"F3.boolean.opBoolean","COPY",FACE,{"derivedFrom":makeQuery(id+"F3.opExtrude","CAP_FACE",FACE,{"disambiguationData":[OSD([subQ5,subQ1,subQ6,subQ7,subQ4,subQ3,subQ2,subQ0])],"isStart":false})})}),makeQuery(id+"F8.opExtrude","SWEPT_FACE",FACE,{"disambiguationData":[OSD([sQuery(id+"F7.wireOp",EDGE,"E67")])]})]});}
            var Q5;
            Q5=makeQuery(id+"F8.boolean.opBoolean","INTERSECT",EDGE,{"disambiguationData":[OD(0.0)],"derivedFrom":[makeQuery(id+"F5.opExtrude","SWEPT_FACE",FACE,{"disambiguationData":[OSD([sQuery(id+"F4.wireOp",EDGE,"E30")])]}),makeQuery(id+"F8.opExtrude","SWEPT_FACE",FACE,{"disambiguationData":[OSD([sQuery(id+"F7.wireOp",EDGE,"E67")])]})]});
            fillet(context, id + "F14", {"entities" : qUnion([Q0, Q1, Q2, Q3, Q4, Q5]), "radius" : 3 * mm, "tangentPropagation" : true, "allowEdgeOverflow" : false});
        }
        {
            var Q0;
            Q0=makeQuery(id+"F1.opExtrude","CAP_EDGE",EDGE,{"disambiguationData":[OSD([sQuery(id+"F0.wireOp",EDGE,"E1.bottom")])],"isStart":false});
            fillet(context, id + "F15", {"entities" : qUnion([Q0]), "radius" : 2 * mm, "tangentPropagation" : true, "allowEdgeOverflow" : false});
        }
        {
            var Q0;
            {var subQ0=sQuery(id+"F0.wireOp",EDGE,"E1.bottom");var subQ1=sQuery(id+"F0.wireOp",EDGE,"E1.top");var subQ2=sQuery(id+"F0.wireOp",EDGE,"E1.left");var subQ3=sQuery(id+"F0.wireOp",EDGE,"E1.right");var subQ4=sQuery(id+"F0.wireOp",EDGE,"E4");var subQ5=sQuery(id+"F0.wireOp",EDGE,"E5");var subQ6=sQuery(id+"F0.wireOp",EDGE,"E6");var subQ7=sQuery(id+"F0.wireOp",EDGE,"E7");var subQ8=sQuery(id+"F0.wireOp",EDGE,"E21.filletArc");var subQ9=sQuery(id+"F0.wireOp",EDGE,"E22.filletArc");var subQ10=sQuery(id+"F0.wireOp",EDGE,"E23.filletArc");var subQ11=sQuery(id+"F0.wireOp",EDGE,"E24.filletArc");Q0=makeQuery(id+"F2.boolean.opBoolean","SPLIT",FACE,{"disambiguationData":[TD([makeQuery(id+"F1.opExtrude","SWEPT_FACE",FACE,{"disambiguationData":[OSD([subQ0])]})])],"derivedFrom":makeQuery(id+"F1.opExtrude","CAP_FACE",FACE,{"disambiguationData":[OSD([subQ0,subQ1,subQ2,subQ3,subQ4,subQ5,subQ6,subQ7,subQ8,subQ9,subQ10,subQ11])],"isStart":true})});}
            var sketch = newSketch(context, id + "F16", { "sketchPlane" : qUnion([Q0])});
            skArc(sketch, "E79.0", {"start": v(154.05, 158.68) * mm, "mid": v(153.04, 163.06) * mm, "end": v(150.2, 166.56) * mm});
            skArc(sketch, "E79.1", {"start": v(14.05, 38.38) * mm, "mid": v(16.98, 31.31) * mm, "end": v(24.05, 28.38) * mm});
            skArc(sketch, "E79.2", {"start": v(34.05, 78.09) * mm, "mid": v(35.06, 73.7) * mm, "end": v(37.9, 70.2) * mm});
            skArc(sketch, "E79.3", {"start": v(174.05, 198.38) * mm, "mid": v(171.12, 205.45) * mm, "end": v(164.05, 208.38) * mm});
            skLineSegment(sketch, "E79.4", {"start": v(14.05, 38.38) * mm, "end": v(14.05, 198.38) * mm});
            skLineSegment(sketch, "E79.5", {"start": v(154.05, 158.68) * mm, "end": v(154.05, 78.09) * mm});
            skCircle(sketch, "E79.6", {"center": v(154.05, 50.88) * mm, "radius": 4 * mm});
            skCircle(sketch, "E79.7", {"center": v(34.05, 185.88) * mm, "radius": 4 * mm});
            skLineSegment(sketch, "E79.8", {"start": v(24.05, 208.38) * mm, "end": v(164.05, 208.38) * mm});
            skArc(sketch, "E79.9", {"start": v(150.2, 70.2) * mm, "mid": v(153.04, 73.7) * mm, "end": v(154.05, 78.09) * mm});
            skLineSegment(sketch, "E79.10", {"start": v(174.05, 38.38) * mm, "end": v(174.05, 198.38) * mm});
            skArc(sketch, "E79.11", {"start": v(37.9, 166.56) * mm, "mid": v(35.06, 163.06) * mm, "end": v(34.05, 158.68) * mm});
            skArc(sketch, "E79.12", {"start": v(37.9, 70.2) * mm, "mid": v(94.05, 50.88) * mm, "end": v(150.2, 70.2) * mm});
            skArc(sketch, "E79.13", {"start": v(164.05, 28.38) * mm, "mid": v(171.12, 31.31) * mm, "end": v(174.05, 38.38) * mm});
            skArc(sketch, "E79.14", {"start": v(24.05, 208.38) * mm, "mid": v(16.98, 205.45) * mm, "end": v(14.05, 198.38) * mm});
            skLineSegment(sketch, "E79.15", {"start": v(24.05, 28.38) * mm, "end": v(164.05, 28.38) * mm});
            skArc(sketch, "E79.16", {"start": v(150.2, 166.56) * mm, "mid": v(94.05, 185.88) * mm, "end": v(37.9, 166.56) * mm});
            skLineSegment(sketch, "E79.17", {"start": v(34.05, 158.68) * mm, "end": v(34.05, 78.09) * mm});
            skCircle(sketch, "E79.18", {"center": v(34.05, 50.88) * mm, "radius": 4 * mm});
            skCircle(sketch, "E79.19", {"center": v(154.05, 185.88) * mm, "radius": 4 * mm});
            skCircle(sketch, "E80", {"center": v(94.05, 238.38) * mm, "radius": 6 * mm});
            skLineSegment(sketch, "E81", {"start": v(61.05, 208.38) * mm, "end": v(79.05, 226.38) * mm});
            skLineSegment(sketch, "E82", {"start": v(109.05, 226.38) * mm, "end": v(127.05, 208.38) * mm});
            skLineSegment(sketch, "E83", {"start": v(109.05, 238.38) * mm, "end": v(109.05, 226.38) * mm});
            skLineSegment(sketch, "E84", {"start": v(79.05, 238.38) * mm, "end": v(79.05, 226.38) * mm});
            skArc(sketch, "E85", {"start": v(109.05, 238.38) * mm, "mid": v(94.05, 253.38) * mm, "end": v(79.05, 238.38) * mm});
            skLineSegment(sketch, "E86", {"start": v(94.05, 208.38) * mm, "end": v(94.05, 238.38) * mm, "construction": true});
            skLineSegment(sketch, "E87", {"start": v(14.05, 118.38) * mm, "end": v(174.05, 118.38) * mm, "construction": true});
            skLineSegment(sketch, "E88.MirrorCS", {"start": v(61.05, 28.38) * mm, "end": v(79.05, 10.38) * mm});
            skLineSegment(sketch, "E89.MirrorCS", {"start": v(79.05, -1.62) * mm, "end": v(79.05, 10.38) * mm});
            skArc(sketch, "E90.MirrorCS", {"start": v(109.05, -1.62) * mm, "mid": v(94.05, -16.62) * mm, "end": v(79.05, -1.62) * mm});
            skLineSegment(sketch, "E91.MirrorCS", {"start": v(94.05, 28.38) * mm, "end": v(94.05, -1.62) * mm, "construction": true});
            skLineSegment(sketch, "E92.MirrorCS", {"start": v(109.05, -1.62) * mm, "end": v(109.05, 10.38) * mm});
            skLineSegment(sketch, "E93.MirrorCS", {"start": v(109.05, 10.38) * mm, "end": v(127.05, 28.38) * mm});
            skCircle(sketch, "E94.MirrorC", {"center": v(94.05, -1.62) * mm, "radius": 6 * mm});
            skSolve(sketch);
        }
        {
            var Q0;
            Q0=makeQuery(id+"F16.imprint","IMPRINT",FACE,{"disambiguationData":[TD([[makeQuery(id+"F16.imprint","IMPRINT",EDGE,{"derivedFrom":sQuery(id+"F16.wireOp",EDGE,"E79.0")}),-1.0]])]});
            var Q1;
            Q1=makeQuery(id+"F16.imprint","IMPRINT",FACE,{"disambiguationData":[TD([[makeQuery(id+"F16.imprint","IMPRINT",EDGE,{"derivedFrom":sQuery(id+"F16.wireOp",EDGE,"E80")}),-1.0]])]});
            var Q2;
            {var subQ1=sQuery(id+"F16.wireOp",EDGE,"E88.MirrorCS");Q2=makeQuery(id+"F16.imprint","IMPRINT",FACE,{"disambiguationData":[TD([[makeQuery(id+"F16.imprint","IMPRINT",EDGE,{"derivedFrom":subQ1}),1.0]])]});}
            var Q3;
            Q3=makeQuery(id+"F2.opExtrude","CAP_FACE",FACE,{"disambiguationData":[OSD([sQuery(id+"F0.wireOp",EDGE,"E12"),sQuery(id+"F0.wireOp",EDGE,"E13"),sQuery(id+"F0.wireOp",EDGE,"E14"),sQuery(id+"F0.wireOp",EDGE,"E15"),sQuery(id+"F0.wireOp",EDGE,"E17.filletArc"),sQuery(id+"F0.wireOp",EDGE,"E18.filletArc"),sQuery(id+"F0.wireOp",EDGE,"E19.filletArc"),sQuery(id+"F0.wireOp",EDGE,"E20.filletArc"),sQuery(id+"F0.wireOp",EDGE,"E25.0"),sQuery(id+"F0.wireOp",EDGE,"E25.1"),sQuery(id+"F0.wireOp",EDGE,"E25.2"),sQuery(id+"F0.wireOp",EDGE,"E25.3"),sQuery(id+"F0.wireOp",EDGE,"E25.4"),sQuery(id+"F0.wireOp",EDGE,"E25.5"),sQuery(id+"F0.wireOp",EDGE,"E25.6"),sQuery(id+"F0.wireOp",EDGE,"E25.7")])],"isStart":false});
            extrude(context, id + "F17", {"entities" : qUnion([Q0, Q1, Q2]), "endBound" : BoundingType.UP_TO_SURFACE, "endBoundEntityFace" : qUnion([Q3]), "depth" : 25.4 * mm});
        }
    });
